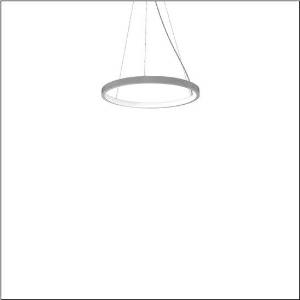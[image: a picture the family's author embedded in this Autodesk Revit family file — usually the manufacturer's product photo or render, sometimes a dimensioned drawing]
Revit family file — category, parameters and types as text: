
# Revit family: silica_21_ring-i_5pjbi1d1204a
name_source: partatom
category: Lighting Fixtures
units: mm (PartAtom-declared; Revit-internal decimal feet)

## family parameters
Cut with Voids When Loaded = No
Host = Face
Light Source = No
Part Type = Normal
Room Calculation Point = No
Round Connector Dimension = Use Diameter
Shared = No

## types (1)
- Silica 21 Ring-I (1 x LED, 3430 lm, 60 W, 3000K)
    Apparent Load = 60 VA
    CIE Flux Codes = 22 48 76 50 101
    Color Rendering = 80
    Color Temperature = 3000K
    Default Elevation = 1800 mm
    Description = Silica 21 Ring-I, suspended luminaire, of PMMA, frosted, light emission: inner ring side luminous distribution, primary light characteristic: symmetric, installation type: suspended mounting, LED, rated luminous flux: 3.430lm, luminous efficacy: 57lm/W, light colour: 830, colour temperature: 3000K, control gear: DALI 2, with terminal, 5-pole, mains connection: 230V, AC/DC, 0/50..60Hz, rated input power: 60W, housing, of extruded aluminium section, metallic grey (RAL 9006), diameter: 610mm, ceiling canopy, metallic grey (RAL 9006), protection rating (lamp compartment): IP40, insulation class (complete): insulation class I (protective earthing), certification: CE, impact resistance: IK02, permissible operating ambient temperature: 0..+35°C, packaging unit: 1 piece
    Height = 48 mm  [stored 0.15748 ft]
    Lamp = 1 x LED
    Lamp Light Flux = 3430 lm
    Lamp Power = 60 W
    Lamp count = 1
    Length = 610 mm
    Luminous efficacy = 57 lm/W
    Manufacturer = Siteco
    ModVariant = No
    Model = 5PJBI1D1204A
    Mounting Place = Ceiling
    Mounting Type = Pendant
    Number of Poles = 1
    OnlyDefault = Yes
    Power Factor = 1
    Product Name = Silica 21 Ring-I
    Product group = suspended luminaire
    ProductGroupID = 904
    Protection Class = Protection class I
    Protection Degree = IP 40
    RLX_Detail_Level = 1
    RLX_Emergency_Light_Flux = 0 lm
    RLX_Emergency_Type = 0
    RLX_Emergency_Type_DB = No
    RlxData = <blob elided: 11493 chars, md5=e04fcbb3>
    Socket = socket
    Standby Power = 0 W
    System Light Flux = 3430 lm
    System Power = 60 W
    Type Comments = Product without accessories
    Type Image = l_1251750.jpg
    URL = http://relux.com
    VarID = ---
    Voltage = 0 V
    Weight = 0.00 kg
    Width = 0 mm  [stored 0 ft]

note: [stored X ft] marks values corroborated as IEEE doubles in the binary element streams (Revit-internal decimal feet)

## geometry (parser evidence)
native form markers: Sweep x11
no freeform markers — native parametric forms only
